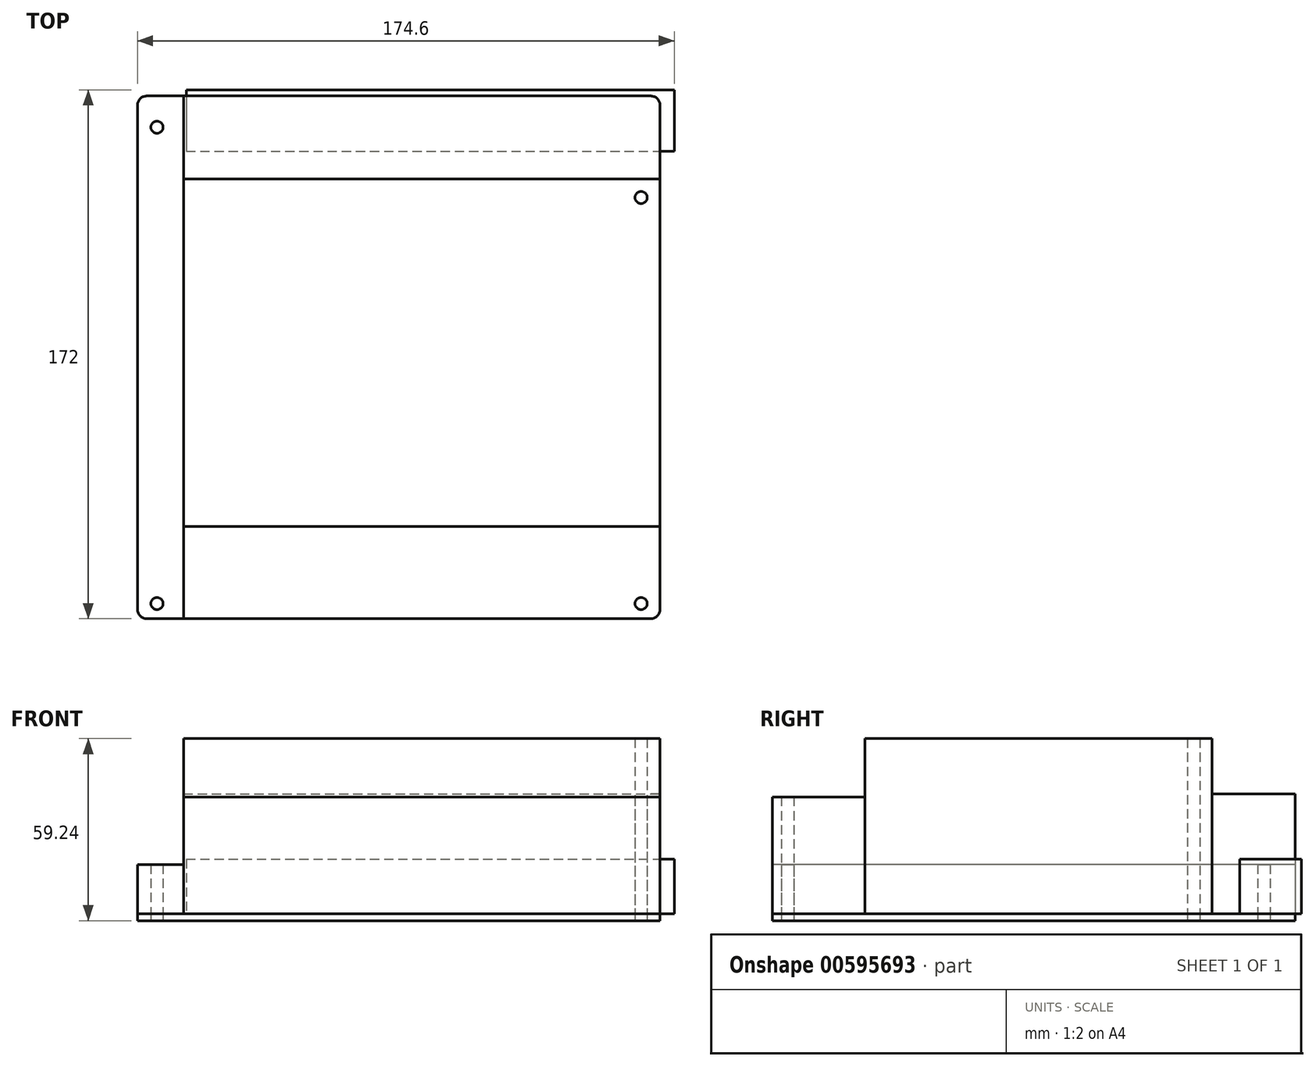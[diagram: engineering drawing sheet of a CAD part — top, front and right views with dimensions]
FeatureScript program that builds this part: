
annotation { "Feature Type Name" : "Feature", "Feature Type Description" : "" }
export const myFeature = defineFeature(function(context is Context, id is Id, definition is map)
    precondition{}
    {
        {
            var Q0;
            Q0=qCreatedBy(makeId("Top.planeOp"),FACE);
            var sketch = newSketch(context, id + "F0", { "sketchPlane" : qUnion([Q0])});
            skLineSegment(sketch, "E0.bottom", {"start": v(-85, 85) * mm, "end": v(85, 85) * mm});
            skLineSegment(sketch, "E0.top", {"start": v(-85, -85) * mm, "end": v(85, -85) * mm});
            skLineSegment(sketch, "E0.left", {"start": v(-85, 85) * mm, "end": v(-85, -85) * mm});
            skLineSegment(sketch, "E0.right", {"start": v(85, 85) * mm, "end": v(85, -85) * mm});
            skLineSegment(sketch, "E1", {"start": v(-85, 85) * mm, "end": v(85, -85) * mm, "construction": true});
            skCircle(sketch, "E2", {"center": v(-78.65, 74.84) * mm, "radius": 1.98 * mm});
            skCircle(sketch, "E3", {"center": v(78.83, 51.98) * mm, "radius": 1.98 * mm});
            skCircle(sketch, "E4", {"center": v(-78.65, -80.1) * mm, "radius": 1.98 * mm});
            skCircle(sketch, "E5", {"center": v(78.83, -80.1) * mm, "radius": 1.98 * mm});
            skSolve(sketch);
        }
        {
            var Q0;
            Q0 = qSketchRegion(id + "F0", true);
            extrude(context, id + "F1", {"entities" : qUnion([Q0]), "depth" : 2.24 * mm, "offsetDistance" : 25 * mm});
        }
        {
            var Q0;
            Q0=makeQuery(id+"F1.opExtrude","SWEPT_EDGE",EDGE,{"disambiguationData":[OSD([sQuery(id+"F0.wireOp",EDGE,"E0.bottom"),sQuery(id+"F0.wireOp",EDGE,"E0.left")])]});
            var Q1;
            Q1=makeQuery(id+"F1.opExtrude","SWEPT_EDGE",EDGE,{"disambiguationData":[OSD([sQuery(id+"F0.wireOp",EDGE,"E0.top"),sQuery(id+"F0.wireOp",EDGE,"E0.left")])]});
            var Q2;
            Q2=makeQuery(id+"F1.opExtrude","SWEPT_EDGE",EDGE,{"disambiguationData":[OSD([sQuery(id+"F0.wireOp",EDGE,"E0.top"),sQuery(id+"F0.wireOp",EDGE,"E0.right")])]});
            var Q3;
            Q3=makeQuery(id+"F1.opExtrude","SWEPT_EDGE",EDGE,{"disambiguationData":[OSD([sQuery(id+"F0.wireOp",EDGE,"E0.bottom"),sQuery(id+"F0.wireOp",EDGE,"E0.right")])]});
            fillet(context, id + "F2", {"entities" : qUnion([Q0, Q1, Q2, Q3]), "radius" : 3 * mm, "tangentPropagation" : true, "allowEdgeOverflow" : false});
        }
        {
            var Q0;
            Q0=makeQuery(id+"F1.opExtrude","CAP_FACE",FACE,{"disambiguationData":[OSD([sQuery(id+"F0.wireOp",EDGE,"E0.bottom"),sQuery(id+"F0.wireOp",EDGE,"E0.top"),sQuery(id+"F0.wireOp",EDGE,"E0.left"),sQuery(id+"F0.wireOp",EDGE,"E0.right"),sQuery(id+"F0.wireOp",EDGE,"E2"),sQuery(id+"F0.wireOp",EDGE,"E3"),sQuery(id+"F0.wireOp",EDGE,"E4"),sQuery(id+"F0.wireOp",EDGE,"E5")])],"isStart":false});
            var sketch = newSketch(context, id + "F3", { "sketchPlane" : qUnion([Q0])});
            skLineSegment(sketch, "E6.bottom", {"start": v(-69.15, 87) * mm, "end": v(89.6, 87) * mm});
            skLineSegment(sketch, "E6.top", {"start": v(-69.15, 67) * mm, "end": v(89.6, 67) * mm});
            skLineSegment(sketch, "E6.left", {"start": v(-69.15, 87) * mm, "end": v(-69.15, 67) * mm});
            skLineSegment(sketch, "E6.right", {"start": v(89.6, 87) * mm, "end": v(89.6, 67) * mm});
            skSolve(sketch);
        }
        {
            var Q0;
            Q0 = qSketchRegion(id + "F3", true);
            extrude(context, id + "F4", {"entities" : qUnion([Q0]), "depth" : (20 - 2.24) * mm, "offsetDistance" : 25 * mm});
        }
        {
            var Q0;
            Q0=makeQuery(id+"F1.opExtrude","CAP_FACE",FACE,{"disambiguationData":[OSD([sQuery(id+"F0.wireOp",EDGE,"E0.bottom"),sQuery(id+"F0.wireOp",EDGE,"E0.top"),sQuery(id+"F0.wireOp",EDGE,"E0.left"),sQuery(id+"F0.wireOp",EDGE,"E0.right"),sQuery(id+"F0.wireOp",EDGE,"E2"),sQuery(id+"F0.wireOp",EDGE,"E3"),sQuery(id+"F0.wireOp",EDGE,"E4"),sQuery(id+"F0.wireOp",EDGE,"E5")])],"isStart":false});
            var sketch = newSketch(context, id + "F5", { "sketchPlane" : qUnion([Q0])});
            skLineSegment(sketch, "E7", {"start": v(-70, 58) * mm, "end": v(85, 58) * mm});
            skLineSegment(sketch, "E8", {"start": v(-70, 85) * mm, "end": v(-70, -85) * mm});
            skLineSegment(sketch, "E9", {"start": v(-70, -55) * mm, "end": v(85, -55) * mm});
            skLineSegment(sketch, "E10.0", {"start": v(-82, 85) * mm, "end": v(82, 85) * mm});
            skLineSegment(sketch, "E11.0.0", {"start": v(-85, 82) * mm, "end": v(-85, -82) * mm});
            skArc(sketch, "E11.0.1", {"start": v(-85, -82) * mm, "mid": v(-84.12, -84.12) * mm, "end": v(-82, -85) * mm});
            skLineSegment(sketch, "E11.0.2", {"start": v(-82, -85) * mm, "end": v(82, -85) * mm});
            skArc(sketch, "E11.0.3", {"start": v(82, -85) * mm, "mid": v(84.12, -84.12) * mm, "end": v(85, -82) * mm});
            skLineSegment(sketch, "E11.0.4", {"start": v(85, -82) * mm, "end": v(85, 82) * mm});
            skArc(sketch, "E11.0.5", {"start": v(85, 82) * mm, "mid": v(84.12, 84.12) * mm, "end": v(82, 85) * mm});
            skLineSegment(sketch, "E11.0.6", {"start": v(82, 85) * mm, "end": v(-82, 85) * mm});
            skArc(sketch, "E11.0.7", {"start": v(-82, 85) * mm, "mid": v(-84.12, 84.12) * mm, "end": v(-85, 82) * mm});
            skSolve(sketch);
        }
        {
            var Q0;
            Q0=makeQuery(id+"F5.imprint","IMPRINT",FACE,{"disambiguationData":[TD([[makeQuery(id+"F5.imprint","IMPRINT",EDGE,{"derivedFrom":sQuery(id+"F5.wireOp",EDGE,"E11.0.0")}),1.0]])]});
            extrude(context, id + "F6", {"entities" : qUnion([Q0]), "depth" : 16 * mm, "offsetDistance" : 25 * mm});
        }
        {
            var Q0;
            {var subQ2=sQuery(id+"F5.wireOp",EDGE,"E7");Q0=makeQuery(id+"F5.imprint","IMPRINT",FACE,{"disambiguationData":[TD([[makeQuery(id+"F5.imprint","IMPRINT",EDGE,{"derivedFrom":subQ2}),1.0]])]});}
            extrude(context, id + "F7", {"entities" : qUnion([Q0]), "depth" : 39 * mm, "offsetDistance" : 25 * mm});
        }
        {
            var Q0;
            {var subQ1=sQuery(id+"F5.wireOp",EDGE,"E9");Q0=makeQuery(id+"F5.imprint","IMPRINT",FACE,{"disambiguationData":[TD([[makeQuery(id+"F5.imprint","IMPRINT",EDGE,{"derivedFrom":subQ1}),-1.0]])]});}
            extrude(context, id + "F8", {"entities" : qUnion([Q0]), "depth" : 38 * mm, "offsetDistance" : 25 * mm});
        }
        {
            var Q0;
            {var subQ1=sQuery(id+"F5.wireOp",EDGE,"E7");Q0=makeQuery(id+"F5.imprint","IMPRINT",FACE,{"disambiguationData":[TD([[makeQuery(id+"F5.imprint","IMPRINT",EDGE,{"derivedFrom":subQ1}),-1.0]])]});}
            extrude(context, id + "F9", {"entities" : qUnion([Q0]), "depth" : 57 * mm, "offsetDistance" : 25 * mm});
        }
    });
